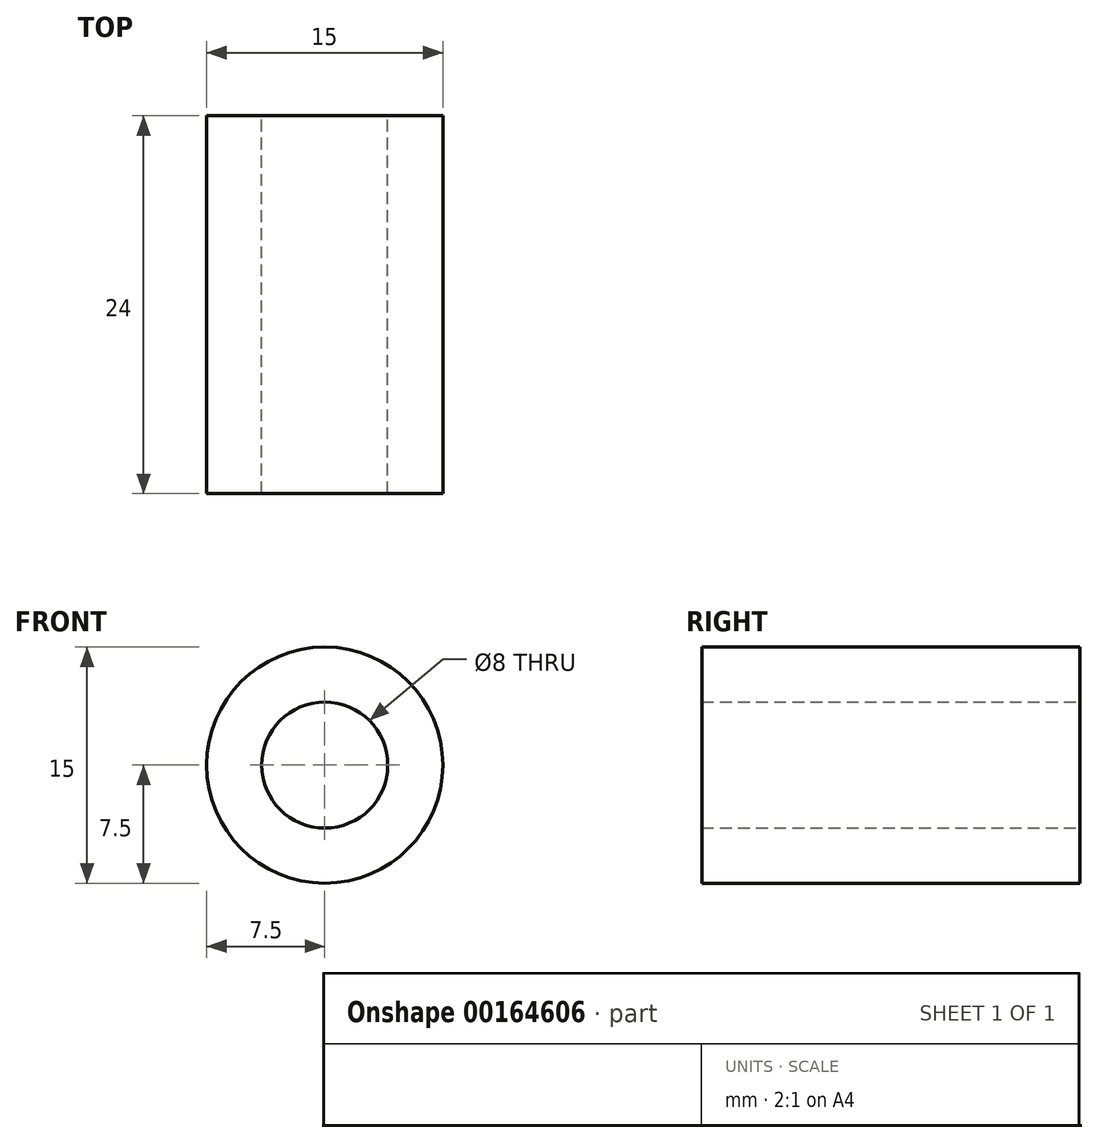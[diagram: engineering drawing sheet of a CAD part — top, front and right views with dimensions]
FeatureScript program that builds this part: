
annotation { "Feature Type Name" : "Feature", "Feature Type Description" : "" }
export const myFeature = defineFeature(function(context is Context, id is Id, definition is map)
    precondition{}
    {
        {
            var Q0;
            Q0=qCreatedBy(makeId("Front.planeOp"),FACE);
            var sketch = newSketch(context, id + "F0", { "sketchPlane" : qUnion([Q0])});
            skCircle(sketch, "E0", {"center": v(0, 0) * mm, "radius": 4 * mm});
            skCircle(sketch, "E1", {"center": v(0, 0) * mm, "radius": 7.5 * mm});
            skSolve(sketch);
        }
        {
            var Q0;
            Q0=makeQuery(id+"F0.imprint","IMPRINT",FACE,{"disambiguationData":[TD([[makeQuery(id+"F0.imprint","IMPRINT",EDGE,{"derivedFrom":sQuery(id+"F0.wireOp",EDGE,"E0")}),-1.0]])]});
            extrude(context, id + "F1", {"entities" : qUnion([Q0]), "endBound" : BoundingType.SYMMETRIC, "depth" : 24 * mm});
        }
    });
